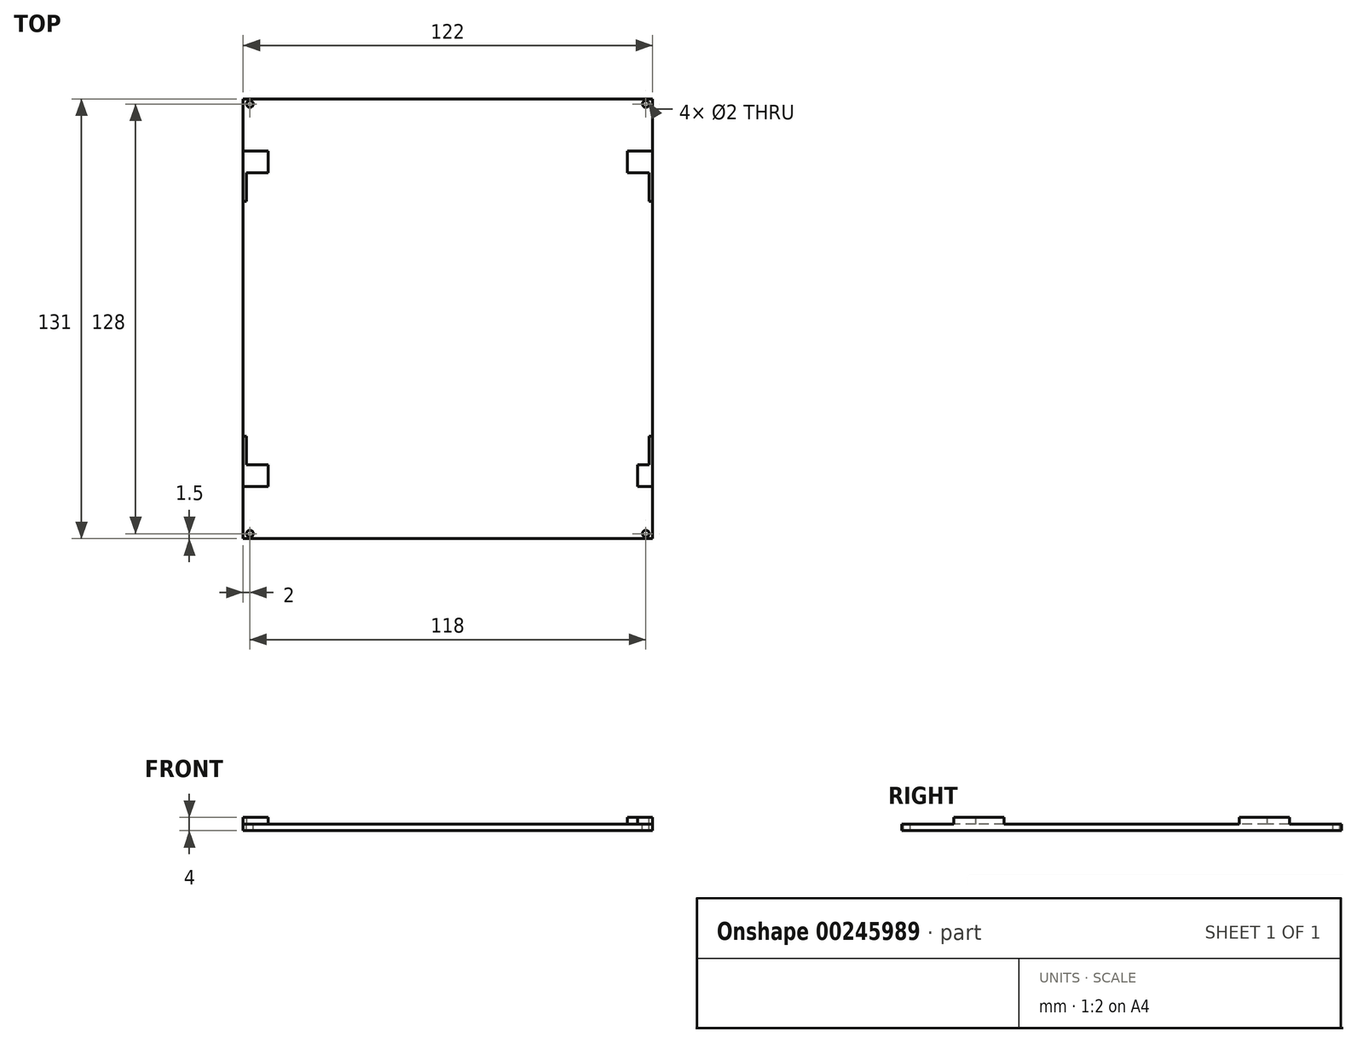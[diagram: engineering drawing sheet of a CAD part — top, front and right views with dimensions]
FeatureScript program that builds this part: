
annotation { "Feature Type Name" : "Feature", "Feature Type Description" : "" }
export const myFeature = defineFeature(function(context is Context, id is Id, definition is map)
    precondition{}
    {
        {
            var Q0;
            Q0=qCreatedBy(makeId("Top.planeOp"),FACE);
            var sketch = newSketch(context, id + "F0", { "sketchPlane" : qUnion([Q0])});
            skLineSegment(sketch, "E0.bottom", {"start": v(-61, 65.5) * mm, "end": v(61, 65.5) * mm});
            skLineSegment(sketch, "E0.top", {"start": v(-61, -65.5) * mm, "end": v(61, -65.5) * mm});
            skLineSegment(sketch, "E0.left", {"start": v(-61, 65.5) * mm, "end": v(-61, -65.5) * mm});
            skLineSegment(sketch, "E0.right", {"start": v(61, 65.5) * mm, "end": v(61, -65.5) * mm});
            skPoint(sketch, "E0.middle", {"position": v(0, 0) * mm});
            skSolve(sketch);
        }
        {
            var Q0;
            Q0=makeQuery(id+"F0.imprint","IMPRINT",FACE,{"disambiguationData":[TD([[makeQuery(id+"F0.imprint","IMPRINT",EDGE,{"derivedFrom":sQuery(id+"F0.wireOp",EDGE,"E0.bottom")}),-1.0]])]});
            extrude(context, id + "F1", {"entities" : qUnion([Q0]), "depth" : 2 * mm});
        }
        {
            var Q0;
            Q0=makeQuery(id+"F1.opExtrude","CAP_FACE",FACE,{"disambiguationData":[OSD([sQuery(id+"F0.wireOp",EDGE,"E0.bottom"),sQuery(id+"F0.wireOp",EDGE,"E0.top"),sQuery(id+"F0.wireOp",EDGE,"E0.left"),sQuery(id+"F0.wireOp",EDGE,"E0.right")])],"isStart":false});
            var sketch = newSketch(context, id + "F2", { "sketchPlane" : qUnion([Q0])});
            skCircle(sketch, "E1", {"center": v(59, 64) * mm, "radius": 1 * mm});
            skCircle(sketch, "E2", {"center": v(59, -64) * mm, "radius": 1 * mm});
            skCircle(sketch, "E3", {"center": v(-59, -64) * mm, "radius": 1 * mm});
            skCircle(sketch, "E4", {"center": v(-59, 64) * mm, "radius": 1 * mm});
            skSolve(sketch);
        }
        {
            var Q0;
            Q0=makeQuery(id+"F2.imprint","IMPRINT",FACE,{"disambiguationData":[TD([[makeQuery(id+"F2.imprint","IMPRINT",EDGE,{"derivedFrom":sQuery(id+"F2.wireOp",EDGE,"E1")}),1.0]])]});
            var Q1;
            Q1=makeQuery(id+"F2.imprint","IMPRINT",FACE,{"disambiguationData":[TD([[makeQuery(id+"F2.imprint","IMPRINT",EDGE,{"derivedFrom":sQuery(id+"F2.wireOp",EDGE,"E2")}),1.0]])]});
            var Q2;
            Q2=makeQuery(id+"F2.imprint","IMPRINT",FACE,{"disambiguationData":[TD([[makeQuery(id+"F2.imprint","IMPRINT",EDGE,{"derivedFrom":sQuery(id+"F2.wireOp",EDGE,"E3")}),1.0]])]});
            var Q3;
            Q3=makeQuery(id+"F2.imprint","IMPRINT",FACE,{"disambiguationData":[TD([[makeQuery(id+"F2.imprint","IMPRINT",EDGE,{"derivedFrom":sQuery(id+"F2.wireOp",EDGE,"E4")}),1.0]])]});
            extrude(context, id + "F3", {"entities" : qUnion([Q0, Q1, Q2, Q3]), "operationType" : NewBodyOperationType.REMOVE, "endBound" : BoundingType.THROUGH_ALL, "oppositeDirection" : true, "depth" : 25 * mm});
        }
        {
            var Q0;
            Q0=makeQuery(id+"F1.opExtrude","CAP_FACE",FACE,{"disambiguationData":[OSD([sQuery(id+"F0.wireOp",EDGE,"E0.bottom"),sQuery(id+"F0.wireOp",EDGE,"E0.top"),sQuery(id+"F0.wireOp",EDGE,"E0.left"),sQuery(id+"F0.wireOp",EDGE,"E0.right")])],"isStart":false});
            var sketch = newSketch(context, id + "F4", { "sketchPlane" : qUnion([Q0])});
            skLineSegment(sketch, "E5.bottom", {"start": v(60, 43.5) * mm, "end": v(-60, 43.5) * mm});
            skLineSegment(sketch, "E5.top", {"start": v(60, -43.5) * mm, "end": v(-60, -43.5) * mm});
            skLineSegment(sketch, "E5.left", {"start": v(60, 43.5) * mm, "end": v(60, -43.5) * mm});
            skLineSegment(sketch, "E5.right", {"start": v(-60, 43.5) * mm, "end": v(-60, -43.5) * mm});
            skPoint(sketch, "E5.middle", {"position": v(0, 0) * mm});
            skSolve(sketch);
        }
        {
            var Q0;
            Q0=makeQuery(id+"F4.imprint","IMPRINT",FACE,{"disambiguationData":[TD([[makeQuery(id+"F4.imprint","IMPRINT",EDGE,{"derivedFrom":sQuery(id+"F4.wireOp",EDGE,"E5.bottom")}),-1.0]])]});
            var sketch = newSketch(context, id + "F5", { "sketchPlane" : qUnion([Q0])});
            skLineSegment(sketch, "E6.bottom", {"start": v(61, 50) * mm, "end": v(-61, 50) * mm});
            skLineSegment(sketch, "E6.top", {"start": v(61, -50) * mm, "end": v(-61, -50) * mm});
            skLineSegment(sketch, "E6.left", {"start": v(61, 50) * mm, "end": v(61, -50) * mm});
            skLineSegment(sketch, "E6.right", {"start": v(-61, 50) * mm, "end": v(-61, -50) * mm});
            skPoint(sketch, "E6.middle", {"position": v(0, 0) * mm});
            skSolve(sketch);
        }
        {
            var Q0;
            Q0=makeQuery(id+"F5.imprint","IMPRINT",FACE,{"disambiguationData":[TD([[makeQuery(id+"F5.imprint","IMPRINT",EDGE,{"derivedFrom":sQuery(id+"F5.wireOp",EDGE,"E6.bottom")}),1.0]])]});
            extrude(context, id + "F6", {"entities" : qUnion([Q0]), "operationType" : NewBodyOperationType.ADD, "depth" : 2 * mm});
        }
        {
            var Q0;
            Q0=makeQuery(id+"F6.opExtrude","CAP_FACE",FACE,{"disambiguationData":[OSD([sQuery(id+"F4.wireOp",EDGE,"E5.bottom"),sQuery(id+"F4.wireOp",EDGE,"E5.top"),sQuery(id+"F4.wireOp",EDGE,"E5.left"),sQuery(id+"F4.wireOp",EDGE,"E5.right"),sQuery(id+"F5.wireOp",EDGE,"E6.bottom"),sQuery(id+"F5.wireOp",EDGE,"E6.top"),sQuery(id+"F5.wireOp",EDGE,"E6.left"),sQuery(id+"F5.wireOp",EDGE,"E6.right")])],"isStart":false});
            var sketch = newSketch(context, id + "F7", { "sketchPlane" : qUnion([Q0])});
            skLineSegment(sketch, "E7.bottom", {"start": v(53.5, 50) * mm, "end": v(-53.5, 50) * mm});
            skLineSegment(sketch, "E7.top", {"start": v(53.5, 43.5) * mm, "end": v(-53.5, 43.5) * mm});
            skLineSegment(sketch, "E7.left", {"start": v(53.5, 50) * mm, "end": v(53.5, 43.5) * mm});
            skLineSegment(sketch, "E7.right", {"start": v(-53.5, 50) * mm, "end": v(-53.5, 43.5) * mm});
            skLineSegment(sketch, "E8.bottom", {"start": v(56.5, -43.5) * mm, "end": v(-53.5, -43.5) * mm});
            skLineSegment(sketch, "E8.top", {"start": v(56.5, -50) * mm, "end": v(-53.5, -50) * mm});
            skLineSegment(sketch, "E8.left", {"start": v(56.5, -43.5) * mm, "end": v(56.5, -50) * mm});
            skLineSegment(sketch, "E8.right", {"start": v(-53.5, -43.5) * mm, "end": v(-53.5, -50) * mm});
            skLineSegment(sketch, "E9.bottom", {"start": v(61, 35) * mm, "end": v(60, 35) * mm});
            skLineSegment(sketch, "E9.top", {"start": v(61, -35) * mm, "end": v(60, -35) * mm});
            skLineSegment(sketch, "E9.left", {"start": v(61, 35) * mm, "end": v(61, -35) * mm});
            skLineSegment(sketch, "E9.right", {"start": v(60, 35) * mm, "end": v(60, -35) * mm});
            skLineSegment(sketch, "E10.bottom", {"start": v(-60, 35) * mm, "end": v(-61, 35) * mm});
            skLineSegment(sketch, "E10.top", {"start": v(-60, -35) * mm, "end": v(-61, -35) * mm});
            skLineSegment(sketch, "E10.left", {"start": v(-60, 35) * mm, "end": v(-60, -35) * mm});
            skLineSegment(sketch, "E10.right", {"start": v(-61, 35) * mm, "end": v(-61, -35) * mm});
            skSolve(sketch);
        }
        {
            var Q0;
            Q0=makeQuery(id+"F7.imprint","IMPRINT",FACE,{"disambiguationData":[TD([[makeQuery(id+"F7.imprint","IMPRINT",EDGE,{"derivedFrom":sQuery(id+"F7.wireOp",EDGE,"E7.bottom")}),1.0]])]});
            var Q1;
            Q1=makeQuery(id+"F7.imprint","IMPRINT",FACE,{"disambiguationData":[TD([[makeQuery(id+"F7.imprint","IMPRINT",EDGE,{"derivedFrom":sQuery(id+"F7.wireOp",EDGE,"E9.bottom")}),1.0]])]});
            var Q2;
            Q2=makeQuery(id+"F7.imprint","IMPRINT",FACE,{"disambiguationData":[TD([[makeQuery(id+"F7.imprint","IMPRINT",EDGE,{"derivedFrom":sQuery(id+"F7.wireOp",EDGE,"E8.bottom")}),1.0]])]});
            var Q3;
            Q3=makeQuery(id+"F7.imprint","IMPRINT",FACE,{"disambiguationData":[TD([[makeQuery(id+"F7.imprint","IMPRINT",EDGE,{"derivedFrom":sQuery(id+"F7.wireOp",EDGE,"E10.bottom")}),1.0]])]});
            extrude(context, id + "F8", {"entities" : qUnion([Q0, Q1, Q2, Q3]), "operationType" : NewBodyOperationType.REMOVE, "oppositeDirection" : true, "depth" : 2 * mm});
        }
    });
